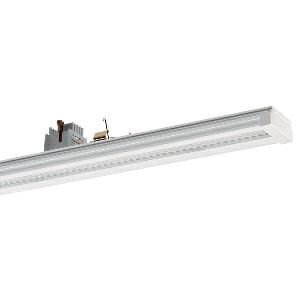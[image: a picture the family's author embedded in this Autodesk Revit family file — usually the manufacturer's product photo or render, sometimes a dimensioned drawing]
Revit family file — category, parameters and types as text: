
# Revit family: conveo_-_cvg_4500_840_xn-l_ea_5_226848439-00804982_b193
name_source: partatom
category: Lighting Fixtures
units: mm (PartAtom-declared; Revit-internal decimal feet)

## family parameters
Cut with Voids When Loaded = No
Host = Face
Light Source = No
Part Type = Normal
Room Calculation Point = No
Round Connector Dimension = Use Diameter
Shared = No

## types (1)
- CONVEO - CVG 4500/840/xN-L/EA/5 (1 x LED, 4650 lm, 4000K)
    Apparent Load = 27 VA
    Approval mark = CE
    CIE Flux Codes = 84 95 99 100 100
    Color Rendering = 80-89
    Color Temperature = 4000K
    Control Gear = Electronic ballast
    Default Elevation = 1800 mm
    Description = CVG 4500/840/xN-L/EA/5|Continuous-row system|light source: LED|work equipment: Electronic ballast|connected load: 220-240 V, 50-60 Hz|Power consumption: approx. 27 W|luminous flux: 4650 lm|luminous efficacy: 172 lm/W|colour temperature: Cold white, ca. 4000 K|color rendering index (CRI): >= 80|chromaticity tolerance:  3 SDCM|System of protection: IP 54|class of protection: I|technology: Switchable|luminaire body|material: Aluminium|surface: Powder coatet|colour: White|lamp cover: Acrylic (PMMA), Satine|weight (net): approx. 1.9 kg|Fastening: Available separately|maximum ambient temperature: 50 ░C|glare control: Lens optics|Approval mark: VDE - ENEC|
    Frequency = 50 Hz
    Height = 70 mm
    Lamp = 1 x LED
    Lamp Light Flux = 4650 lm
    Lamp count = 1
    Length = 1500 mm
    Luminous efficacy = 172 lm/W
    Manufacturer = Waldmann
    ModVariant = No
    Model = 226848439-00804982
    Mounting Place = Ceiling
    Mounting Type = Pendant
    Number of Poles = 1
    OnlyDefault = Yes
    Power Factor = 1
    Product Name = CONVEO - CVG 4500/840/xN-L/EA/5
    Product group = Continuous-row system (industry)
    ProductGroupID = 301
    Protection Class = Protection class I
    Protection Degree = IP 54
    RLX_Detail_Level = 1
    RlxData = <blob elided: 100485 chars, md5=6f39bf2a>
    Socket = socket
    Standby Power = 0 W
    System Light Flux = 4650 lm
    System Power = 27 W
    Type Comments = Product without accessories
    Type Image = 226848319-00804970_1l5.jpg
    URL = http://relux.com
    VarID = ---
    Voltage = 230 V
    Voltage Range = 220-240 V
    Weight = 0.00 kg
    Width = 64 mm

## geometry (parser evidence)
native form markers: Blend x4, Sweep x10
no freeform markers — native parametric forms only
